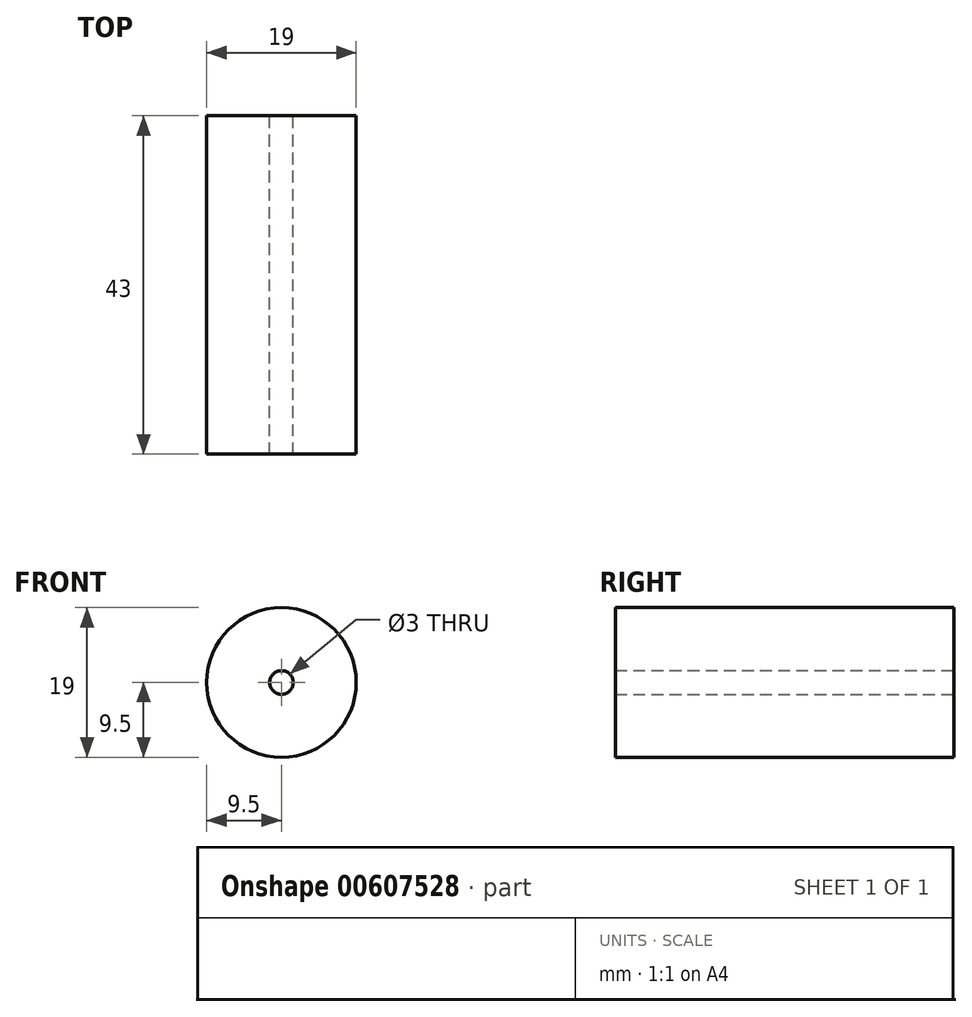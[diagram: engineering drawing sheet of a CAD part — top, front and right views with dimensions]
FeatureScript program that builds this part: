
annotation { "Feature Type Name" : "Feature", "Feature Type Description" : "" }
export const myFeature = defineFeature(function(context is Context, id is Id, definition is map)
    precondition{}
    {
        {
            var Q0;
            Q0=qCreatedBy(makeId("Front.planeOp"),FACE);
            var sketch = newSketch(context, id + "F0", { "sketchPlane" : qUnion([Q0])});
            skCircle(sketch, "E0", {"center": v(0, 0) * mm, "radius": 9.5 * mm});
            skSolve(sketch);
        }
        {
            var Q0;
            Q0=makeQuery(id+"F0.imprint","IMPRINT",FACE,{"disambiguationData":[TD([[makeQuery(id+"F0.imprint","IMPRINT",EDGE,{"derivedFrom":sQuery(id+"F0.wireOp",EDGE,"E0")}),1.0]])]});
            extrude(context, id + "F1", {"entities" : qUnion([Q0]), "depth" : 43 * mm, "offsetDistance" : 25.4 * mm});
        }
        {
            var Q0;
            Q0=qCreatedBy(makeId("Front.planeOp"),FACE);
            var sketch = newSketch(context, id + "F2", { "sketchPlane" : qUnion([Q0])});
            skCircle(sketch, "E1", {"center": v(0, 0) * mm, "radius": 1.5 * mm});
            skSolve(sketch);
        }
        {
            var Q0;
            Q0=sQuery(id+"F2.wireOp",VERTEX,"E1.center");
            var Q1;
            Q1=makeQuery(id+"F1.opExtrude","SWEPT_BODY",BODY,{"disambiguationData":[OSD([sQuery(id+"F0.wireOp",EDGE,"E0")])]});
            hole(context, id + "F3", {"style" : HoleStyle.SIMPLE, "endStyle" : HoleEndStyle.THROUGH, "oppositeDirection" : true, "holeDiameter" : 3 * mm, "majorDiameter" : 6.35 * mm, "isTappedThrough" : true, "tappedDepth" : 12.7 * mm, "tapClearance" : 3, "locations" : qUnion([Q0]), "scope" : qUnion([Q1])});
        }
    });
